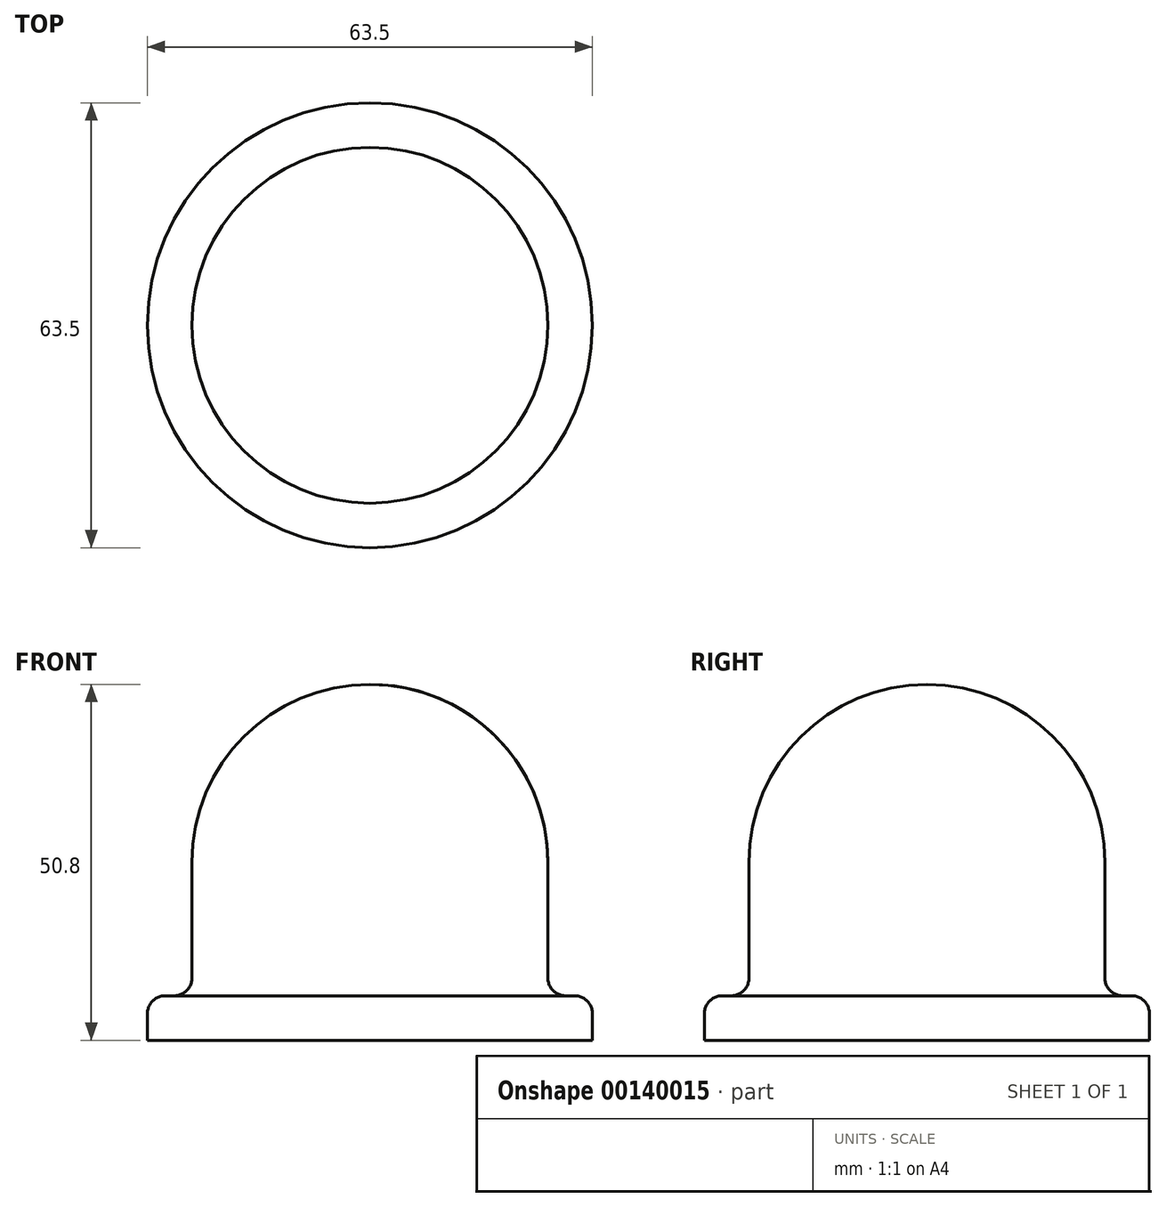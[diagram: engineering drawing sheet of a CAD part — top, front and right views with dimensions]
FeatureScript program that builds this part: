
annotation { "Feature Type Name" : "Feature", "Feature Type Description" : "" }
export const myFeature = defineFeature(function(context is Context, id is Id, definition is map)
    precondition{}
    {
        {
            var Q0;
            Q0=qCreatedBy(makeId("Front.planeOp"),FACE);
            var sketch = newSketch(context, id + "F0", { "sketchPlane" : qUnion([Q0])});
            skLineSegment(sketch, "E0", {"start": v(0, 25.4) * mm, "end": v(0, -25.4) * mm});
            skArc(sketch, "E1", {"start": v(0, 25.4) * mm, "mid": v(17.96, 17.96) * mm, "end": v(25.4, 0) * mm});
            skLineSegment(sketch, "E2", {"start": v(25.4, 0) * mm, "end": v(25.4, -25.4) * mm});
            skLineSegment(sketch, "E3", {"start": v(25.4, -25.4) * mm, "end": v(0, -25.4) * mm});
            skSolve(sketch);
        }
        {
            var Q0;
            Q0 = qSketchRegion(id + "F0", true);
            var Q1;
            Q1=sQuery(id+"F0.wireOp",EDGE,"E0");
            revolve(context, id + "F1", {"entities" : qUnion([Q0]), "axis" : qUnion([Q1]), "revolveType" : RevolveType.FULL});
        }
        {
            var Q0;
            Q0=makeQuery(id+"F1.opRevolve","SWEPT_FACE",FACE,{"disambiguationData":[OSD([sQuery(id+"F0.wireOp",EDGE,"E3")])]});
            var sketch = newSketch(context, id + "F2", { "sketchPlane" : qUnion([Q0])});
            skCircle(sketch, "E4", {"center": v(0, 0) * mm, "radius": 31.75 * mm});
            skSolve(sketch);
        }
        {
            var Q0;
            Q0 = qSketchRegion(id + "F2", true);
            extrude(context, id + "F3", {"entities" : qUnion([Q0]), "operationType" : NewBodyOperationType.ADD, "oppositeDirection" : true, "depth" : 6.35 * mm});
        }
        {
            var Q0;
            Q0=makeQuery(id+"F3.boolean.opBoolean","INTERSECT",EDGE,{"derivedFrom":[makeQuery(id+"F1.opRevolve","SWEPT_FACE",FACE,{"disambiguationData":[OSD([sQuery(id+"F0.wireOp",EDGE,"E2")])]}),makeQuery(id+"F3.opExtrude","CAP_FACE",FACE,{"disambiguationData":[OSD([sQuery(id+"F2.wireOp",EDGE,"E4")])],"isStart":false})]});
            var Q1;
            Q1=makeQuery(id+"F3.opExtrude","CAP_EDGE",EDGE,{"disambiguationData":[OSD([sQuery(id+"F2.wireOp",EDGE,"E4")])],"isStart":false});
            var Q2;
            Q2=makeQuery(id+"F1.opRevolve","SWEPT_EDGE",EDGE,{"disambiguationData":[OSD([sQuery(id+"F0.wireOp",EDGE,"E1"),sQuery(id+"F0.wireOp",EDGE,"E2")])]});
            fillet(context, id + "F4", {"entities" : qUnion([Q0, Q1, Q2]), "radius" : 2.54 * mm, "tangentPropagation" : true, "allowEdgeOverflow" : false});
        }
    });
